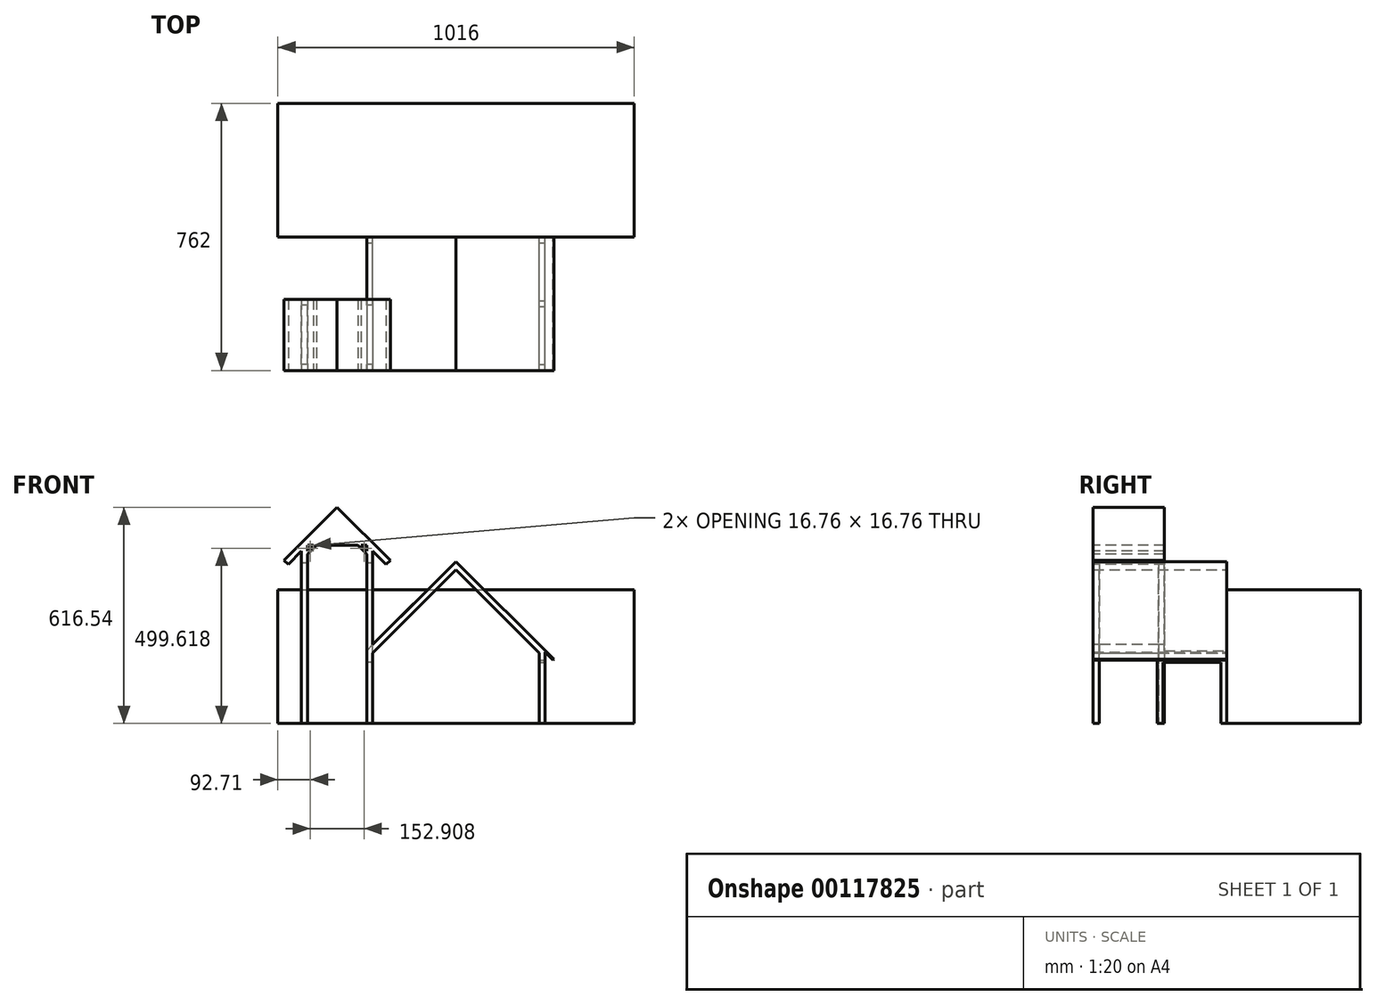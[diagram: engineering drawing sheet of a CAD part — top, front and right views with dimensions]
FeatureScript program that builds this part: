
annotation { "Feature Type Name" : "Feature", "Feature Type Description" : "" }
export const myFeature = defineFeature(function(context is Context, id is Id, definition is map)
    precondition{}
    {
        {
            var Q0;
            Q0=qCreatedBy(makeId("Front.planeOp"),FACE);
            var sketch = newSketch(context, id + "F0", { "sketchPlane" : qUnion([Q0])});
            skLineSegment(sketch, "E0.bottom", {"start": v(0, 0) * mm, "end": v(508, 0) * mm});
            skLineSegment(sketch, "E0.top", {"start": v(0, 381) * mm, "end": v(508, 381) * mm});
            skLineSegment(sketch, "E0.left", {"start": v(0, 0) * mm, "end": v(0, 381) * mm});
            skLineSegment(sketch, "E0.right", {"start": v(508, 0) * mm, "end": v(508, 381) * mm});
            skLineSegment(sketch, "E1.MirrorCS", {"start": v(0, 0) * mm, "end": v(-508, 0) * mm});
            skLineSegment(sketch, "E2.MirrorCS", {"start": v(-508, 0) * mm, "end": v(-508, 381) * mm});
            skLineSegment(sketch, "E3.MirrorCS", {"start": v(0, 381) * mm, "end": v(-508, 381) * mm});
            skSolve(sketch);
        }
        {
            var Q0;
            Q0=makeQuery(id+"F0.imprint","IMPRINT",FACE,{"disambiguationData":[TD([[makeQuery(id+"F0.imprint","IMPRINT",EDGE,{"derivedFrom":sQuery(id+"F0.wireOp",EDGE,"E0.bottom")}),1.0]])]});
            var Q1;
            Q1=makeQuery(id+"F0.imprint","IMPRINT",FACE,{"disambiguationData":[TD([[makeQuery(id+"F0.imprint","IMPRINT",EDGE,{"derivedFrom":sQuery(id+"F0.wireOp",EDGE,"E0.left")}),1.0]])]});
            extrude(context, id + "F1", {"entities" : qUnion([Q0, Q1]), "oppositeDirection" : true, "depth" : 381 * mm});
        }
        {
            var Q0;
            Q0=qCreatedBy(makeId("Front.planeOp"),FACE);
            var sketch = newSketch(context, id + "F2", { "sketchPlane" : qUnion([Q0])});
            skLineSegment(sketch, "E4", {"start": v(254, 0) * mm, "end": v(254, 203.2) * mm});
            skLineSegment(sketch, "E5", {"start": v(254, 203.2) * mm, "end": v(276.57, 180.63) * mm});
            skLineSegment(sketch, "E6.3", {"start": v(-501.65, 374.65) * mm, "end": v(-501.65, 6.35) * mm});
            skLineSegment(sketch, "E7", {"start": v(276.57, 180.63) * mm, "end": v(278.82, 182.87) * mm});
            skLineSegment(sketch, "E8.MirrorCS", {"start": v(-254, 207.7) * mm, "end": v(0, 461.7) * mm});
            skLineSegment(sketch, "E9", {"start": v(-254, 0) * mm, "end": v(-237.24, 0) * mm});
            skLineSegment(sketch, "E10.MirrorCS", {"start": v(237.24, 200.75) * mm, "end": v(152.4, 285.58) * mm});
            skLineSegment(sketch, "E11", {"start": v(237.24, 200.75) * mm, "end": v(237.24, 0) * mm});
            skLineSegment(sketch, "E12", {"start": v(237.24, 0) * mm, "end": v(254, 0) * mm});
            skLineSegment(sketch, "E13", {"start": v(0, 461.7) * mm, "end": v(278.82, 182.87) * mm});
            skLineSegment(sketch, "E14", {"start": v(-254, 207.7) * mm, "end": v(-254, 0) * mm});
            skLineSegment(sketch, "E15", {"start": v(152.4, 285.58) * mm, "end": v(0, 437.98) * mm});
            skLineSegment(sketch, "E16", {"start": v(0, 437.98) * mm, "end": v(-237.24, 200.75) * mm});
            skLineSegment(sketch, "E17", {"start": v(-237.24, 200.75) * mm, "end": v(-237.24, 0) * mm});
            skSolve(sketch);
        }
        {
            var Q0;
            {var subQ1=sQuery(id+"F2.wireOp",EDGE,"E5");Q0=makeQuery(id+"F2.imprint","IMPRINT",FACE,{"disambiguationData":[TD([[makeQuery(id+"F2.imprint","IMPRINT",EDGE,{"derivedFrom":subQ1}),1.0]])]});}
            extrude(context, id + "F3", {"entities" : qUnion([Q0]), "operationType" : NewBodyOperationType.ADD, "depth" : 381 * mm});
        }
        {
            var Q0;
            Q0=makeQuery(id+"F3.opExtrude","SWEPT_FACE",FACE,{"disambiguationData":[OSD([sQuery(id+"F2.wireOp",EDGE,"E4")])]});
            var sketch = newSketch(context, id + "F4", { "sketchPlane" : qUnion([Q0])});
            skLineSegment(sketch, "E18", {"start": v(-381, 0) * mm, "end": v(-364.1, 0) * mm});
            skLineSegment(sketch, "E19", {"start": v(-364.1, 0) * mm, "end": v(-364.1, 180.6) * mm});
            skLineSegment(sketch, "E20", {"start": v(0, 0) * mm, "end": v(0, 174.24) * mm});
            skLineSegment(sketch, "E21", {"start": v(0, 174.24) * mm, "end": v(-16.9, 174.24) * mm});
            skLineSegment(sketch, "E22", {"start": v(-16.9, 174.24) * mm, "end": v(-16.9, 0) * mm});
            skPoint(sketch, "E23.endSnap0", {"position": v(-190.5, 93.47) * mm});
            skLineSegment(sketch, "E24", {"start": v(-198.95, 180.6) * mm, "end": v(-198.95, 0) * mm});
            skLineSegment(sketch, "E25.MirrorCS", {"start": v(-182.05, 174.24) * mm, "end": v(-182.05, 0) * mm});
            skLineSegment(sketch, "E26", {"start": v(-364.1, 180.6) * mm, "end": v(-198.95, 180.6) * mm});
            skLineSegment(sketch, "E27", {"start": v(-364.1, 0) * mm, "end": v(-198.95, 0) * mm});
            skLineSegment(sketch, "E28", {"start": v(-182.05, 174.24) * mm, "end": v(-16.9, 174.24) * mm});
            skLineSegment(sketch, "E29", {"start": v(-182.05, 0) * mm, "end": v(-16.9, 0) * mm});
            skSolve(sketch);
        }
        {
            var Q0;
            Q0=makeQuery(id+"F4.imprint","IMPRINT",FACE,{"disambiguationData":[TD([[makeQuery(id+"F4.imprint","IMPRINT",EDGE,{"derivedFrom":sQuery(id+"F4.wireOp",EDGE,"E19")}),-1.0]])]});
            var Q1;
            Q1=makeQuery(id+"F4.imprint","IMPRINT",FACE,{"disambiguationData":[TD([[makeQuery(id+"F4.imprint","IMPRINT",EDGE,{"derivedFrom":sQuery(id+"F4.wireOp",EDGE,"E22")}),-1.0]])]});
            extrude(context, id + "F5", {"entities" : qUnion([Q0, Q1]), "operationType" : NewBodyOperationType.REMOVE, "endBound" : BoundingType.THROUGH_ALL, "oppositeDirection" : true, "depth" : 25.4 * mm});
        }
        {
            var Q0;
            Q0=qCreatedBy(makeId("Front.planeOp"),FACE);
            cPlane(context, id + "F6", {"entities" : qUnion([Q0]), "cplaneType" : CPlaneType.OFFSET, "offset" : 381 * mm, "width" : 152.4 * mm, "height" : 152.4 * mm});
        }
        {
            var Q0;
            Q0=qCreatedBy(id+"F6.planeOp",FACE);
            var sketch = newSketch(context, id + "F7", { "sketchPlane" : qUnion([Q0])});
            skLineSegment(sketch, "E30", {"start": v(0, 0) * mm, "end": v(-254, 0) * mm});
            skLineSegment(sketch, "E31", {"start": v(-254, 0) * mm, "end": v(-254, 482.26) * mm});
            skLineSegment(sketch, "E32", {"start": v(-254, 508) * mm, "end": v(-270.76, 508) * mm});
            skLineSegment(sketch, "E33", {"start": v(-423.67, 482.26) * mm, "end": v(-423.67, 0) * mm});
            skLineSegment(sketch, "E34", {"start": v(-440.44, 491.24) * mm, "end": v(-478.28, 453.4) * mm});
            skLineSegment(sketch, "E35", {"start": v(-338.84, 508) * mm, "end": v(-338.84, 760.08) * mm});
            skLineSegment(sketch, "E36.0", {"start": v(-435.53, 519.85) * mm, "end": v(-490.13, 465.25) * mm});
            skLineSegment(sketch, "E37", {"start": v(-435.53, 519.85) * mm, "end": v(-338.84, 616.54) * mm});
            skLineSegment(sketch, "E38", {"start": v(-490.13, 465.25) * mm, "end": v(-478.28, 453.4) * mm});
            skLineSegment(sketch, "E39.0", {"start": v(-440.44, 491.24) * mm, "end": v(-440.44, 0) * mm});
            skLineSegment(sketch, "E40.MirrorCS", {"start": v(-242.15, 519.85) * mm, "end": v(-338.84, 616.54) * mm});
            skLineSegment(sketch, "E41.MirrorCS", {"start": v(-242.15, 519.85) * mm, "end": v(-187.54, 465.25) * mm});
            skLineSegment(sketch, "E42.MirrorCS", {"start": v(-237.24, 491.24) * mm, "end": v(-199.4, 453.4) * mm});
            skLineSegment(sketch, "E43.MirrorCS", {"start": v(-187.54, 465.25) * mm, "end": v(-199.4, 453.4) * mm});
            skLineSegment(sketch, "E44", {"start": v(-237.24, 491.24) * mm, "end": v(-237.24, 0) * mm});
            skLineSegment(sketch, "E45", {"start": v(-440.44, 0) * mm, "end": v(-423.67, 0) * mm});
            skLineSegment(sketch, "E46", {"start": v(-347.22, 457.2) * mm, "end": v(-347.22, 406.4) * mm});
            skLineSegment(sketch, "E47", {"start": v(-347.22, 406.4) * mm, "end": v(-385.32, 406.4) * mm});
            skLineSegment(sketch, "E48", {"start": v(-385.32, 406.4) * mm, "end": v(-385.32, 389.64) * mm});
            skLineSegment(sketch, "E49", {"start": v(-385.32, 389.64) * mm, "end": v(-347.22, 389.64) * mm});
            skLineSegment(sketch, "E50", {"start": v(-347.22, 389.64) * mm, "end": v(-347.22, 254) * mm});
            skLineSegment(sketch, "E51", {"start": v(-347.22, 254) * mm, "end": v(-338.84, 254) * mm});
            skLineSegment(sketch, "E52", {"start": v(-347.22, 457.2) * mm, "end": v(-330.45, 457.2) * mm});
            skLineSegment(sketch, "E53", {"start": v(-338.84, 508) * mm, "end": v(-338.84, 457.2) * mm});
            skLineSegment(sketch, "E54.MirrorCS", {"start": v(-330.45, 457.2) * mm, "end": v(-330.45, 406.4) * mm});
            skLineSegment(sketch, "E55.MirrorCS", {"start": v(-330.45, 406.4) * mm, "end": v(-292.35, 406.4) * mm});
            skLineSegment(sketch, "E56.MirrorCS", {"start": v(-292.35, 406.4) * mm, "end": v(-292.35, 389.64) * mm});
            skLineSegment(sketch, "E57.MirrorCS", {"start": v(-292.35, 389.64) * mm, "end": v(-330.45, 389.64) * mm});
            skLineSegment(sketch, "E58.MirrorCS", {"start": v(-330.45, 389.64) * mm, "end": v(-330.45, 254) * mm});
            skLineSegment(sketch, "E59.MirrorCS", {"start": v(-330.45, 254) * mm, "end": v(-338.84, 254) * mm});
            skLineSegment(sketch, "E60", {"start": v(-423.67, 491.24) * mm, "end": v(-406.9, 508) * mm});
            skLineSegment(sketch, "E61.0", {"start": v(-419.18, 486.75) * mm, "end": v(-402.42, 503.5) * mm});
            skLineSegment(sketch, "E62", {"start": v(-402.42, 503.5) * mm, "end": v(-397.93, 508) * mm});
            skLineSegment(sketch, "E63", {"start": v(-419.18, 486.75) * mm, "end": v(-423.67, 482.26) * mm});
            skPoint(sketch, "E64.orphan", {"position": v(-423.67, 508) * mm});
            skLineSegment(sketch, "E65", {"start": v(-423.67, 491.24) * mm, "end": v(-423.67, 508) * mm});
            skLineSegment(sketch, "E66", {"start": v(-423.67, 508) * mm, "end": v(-406.9, 508) * mm});
            skLineSegment(sketch, "E67.MirrorCS", {"start": v(-258.5, 486.75) * mm, "end": v(-254, 482.26) * mm});
            skLineSegment(sketch, "E68.MirrorCS", {"start": v(-258.5, 486.75) * mm, "end": v(-275.25, 503.5) * mm});
            skLineSegment(sketch, "E69.MirrorCS", {"start": v(-275.25, 503.5) * mm, "end": v(-279.74, 508) * mm});
            skLineSegment(sketch, "E70.MirrorCS", {"start": v(-254, 491.24) * mm, "end": v(-270.76, 508) * mm});
            skLineSegment(sketch, "E71.MirrorCS", {"start": v(-254, 491.24) * mm, "end": v(-254, 508) * mm});
            skLineSegment(sketch, "E72.trimOffspring", {"start": v(-279.74, 508) * mm, "end": v(-397.93, 508) * mm});
            skSolve(sketch);
        }
        {
            var Q0;
            Q0=makeQuery(id+"F7.imprint","IMPRINT",FACE,{"disambiguationData":[TD([[makeQuery(id+"F7.imprint","IMPRINT",EDGE,{"derivedFrom":sQuery(id+"F7.wireOp",EDGE,"E33")}),-1.0]])]});
            var Q1;
            {var subQ0=sQuery(id+"F7.wireOp",EDGE,"E38");Q1=makeQuery(id+"F7.imprint","IMPRINT",FACE,{"disambiguationData":[TD([[makeQuery(id+"F7.imprint","IMPRINT",EDGE,{"derivedFrom":subQ0}),1.0]])]});}
            var Q2;
            {var subQ1=sQuery(id+"F7.wireOp",EDGE,"E31");Q2=makeQuery(id+"F7.imprint","IMPRINT",FACE,{"disambiguationData":[TD([[makeQuery(id+"F7.imprint","IMPRINT",EDGE,{"derivedFrom":subQ1}),-1.0]])]});}
            var Q3;
            {var subQ2=sQuery(id+"F7.wireOp",EDGE,"E46");Q3=makeQuery(id+"F7.imprint","IMPRINT",FACE,{"disambiguationData":[TD([[makeQuery(id+"F7.imprint","IMPRINT",EDGE,{"derivedFrom":subQ2}),1.0]])]});}
            extrude(context, id + "F8", {"entities" : qUnion([Q0, Q1, Q2, Q3]), "operationType" : NewBodyOperationType.ADD, "oppositeDirection" : true, "depth" : 203.2 * mm});
        }
        {
            var Q0;
            Q0=makeQuery(id+"F8.opExtrude","SWEPT_FACE",FACE,{"disambiguationData":[OSD([sQuery(id+"F7.wireOp",EDGE,"E39.0")])]});
            var sketch = newSketch(context, id + "F9", { "sketchPlane" : qUnion([Q0])});
            skLineSegment(sketch, "E73", {"start": v(381, 0) * mm, "end": v(364.24, 0) * mm});
            skLineSegment(sketch, "E74", {"start": v(364.24, 0) * mm, "end": v(364.24, 457.2) * mm});
            skLineSegment(sketch, "E75", {"start": v(364.24, 457.2) * mm, "end": v(194.56, 457.2) * mm});
            skLineSegment(sketch, "E76", {"start": v(194.56, 457.2) * mm, "end": v(194.56, 0) * mm});
            skLineSegment(sketch, "E77", {"start": v(194.56, 0) * mm, "end": v(177.8, 0) * mm});
            skLineSegment(sketch, "E78", {"start": v(194.56, 0) * mm, "end": v(364.24, 0) * mm});
            skSolve(sketch);
        }
        {
            var Q0;
            Q0=makeQuery(id+"F9.imprint","IMPRINT",FACE,{"disambiguationData":[TD([[makeQuery(id+"F9.imprint","IMPRINT",EDGE,{"derivedFrom":sQuery(id+"F9.wireOp",EDGE,"E74")}),1.0]])]});
            extrude(context, id + "F10", {"entities" : qUnion([Q0]), "operationType" : NewBodyOperationType.REMOVE, "oppositeDirection" : true, "depth" : 203.2 * mm});
        }
        {
            var Q0;
            Q0=makeQuery(id+"F10.boolean.opBoolean","SPLIT",BODY,{"disambiguationData":[OD(1.0)],"derivedFrom":makeQuery(id+"F8.opExtrude","SWEPT_BODY",BODY,{"disambiguationData":[OSD([sQuery(id+"F7.wireOp",EDGE,"E46"),sQuery(id+"F7.wireOp",EDGE,"E47"),sQuery(id+"F7.wireOp",EDGE,"E48"),sQuery(id+"F7.wireOp",EDGE,"E49"),sQuery(id+"F7.wireOp",EDGE,"E50"),sQuery(id+"F7.wireOp",EDGE,"E51"),sQuery(id+"F7.wireOp",EDGE,"E52"),sQuery(id+"F7.wireOp",EDGE,"E54.MirrorCS"),sQuery(id+"F7.wireOp",EDGE,"E55.MirrorCS"),sQuery(id+"F7.wireOp",EDGE,"E56.MirrorCS"),sQuery(id+"F7.wireOp",EDGE,"E57.MirrorCS"),sQuery(id+"F7.wireOp",EDGE,"E58.MirrorCS"),sQuery(id+"F7.wireOp",EDGE,"E59.MirrorCS")])]})});
            deleteBodies(context, id + "F11", {"entities" : qUnion([Q0])});
        }
    });
